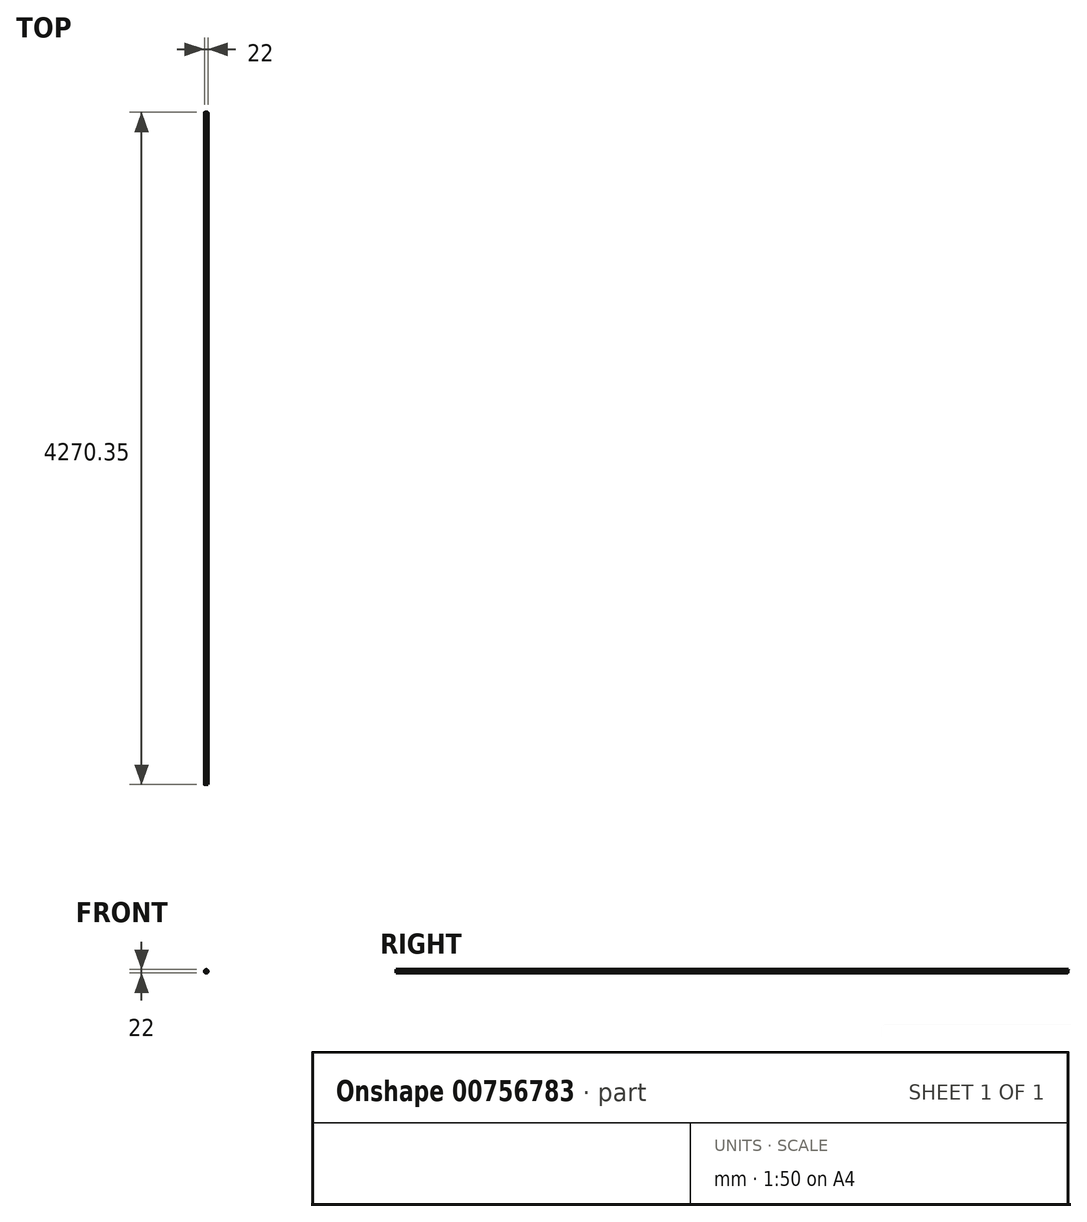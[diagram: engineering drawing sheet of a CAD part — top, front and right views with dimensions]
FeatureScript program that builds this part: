
annotation { "Feature Type Name" : "Feature", "Feature Type Description" : "" }
export const myFeature = defineFeature(function(context is Context, id is Id, definition is map)
    precondition{}
    {
        {
            var Q0;
            Q0=qCreatedBy(makeId("Front.planeOp"),FACE);
            var sketch = newSketch(context, id + "F0", { "sketchPlane" : qUnion([Q0])});
            skCircle(sketch, "E0", {"center": v(0, 0) * mm, "radius": 11 * mm});
            skSolve(sketch);
        }
        {
            var Q0;
            Q0=makeQuery(id+"F0.imprint","IMPRINT",FACE,{"disambiguationData":[TD([[makeQuery(id+"F0.imprint","IMPRINT",EDGE,{"derivedFrom":sQuery(id+"F0.wireOp",EDGE,"E0")}),1.0]])]});
            extrude(context, id + "F1", {"entities" : qUnion([Q0]), "depth" : 4270.35 * mm, "offsetDistance" : 25 * mm});
        }
        {
            var Q0;
            Q0=qCreatedBy(makeId("Right.planeOp"),FACE);
            var sketch = newSketch(context, id + "F2", { "sketchPlane" : qUnion([Q0])});
            skLineSegment(sketch, "E1.0", {"start": v(0, -11) * mm, "end": v(0, 11) * mm});
            skLineSegment(sketch, "E2", {"start": v(0, -11) * mm, "end": v(-4270.35, -11) * mm});
            skLineSegment(sketch, "E3", {"start": v(0, 11) * mm, "end": v(-2.7, -11) * mm});
            skSolve(sketch);
        }
        {
            var Q0;
            Q0 = qSketchRegion(id + "F2", true);
            extrude(context, id + "F3", {"entities" : qUnion([Q0]), "operationType" : NewBodyOperationType.REMOVE, "endBound" : BoundingType.SYMMETRIC, "oppositeDirection" : true, "depth" : 25 * mm, "offsetDistance" : 25 * mm});
        }
    });
